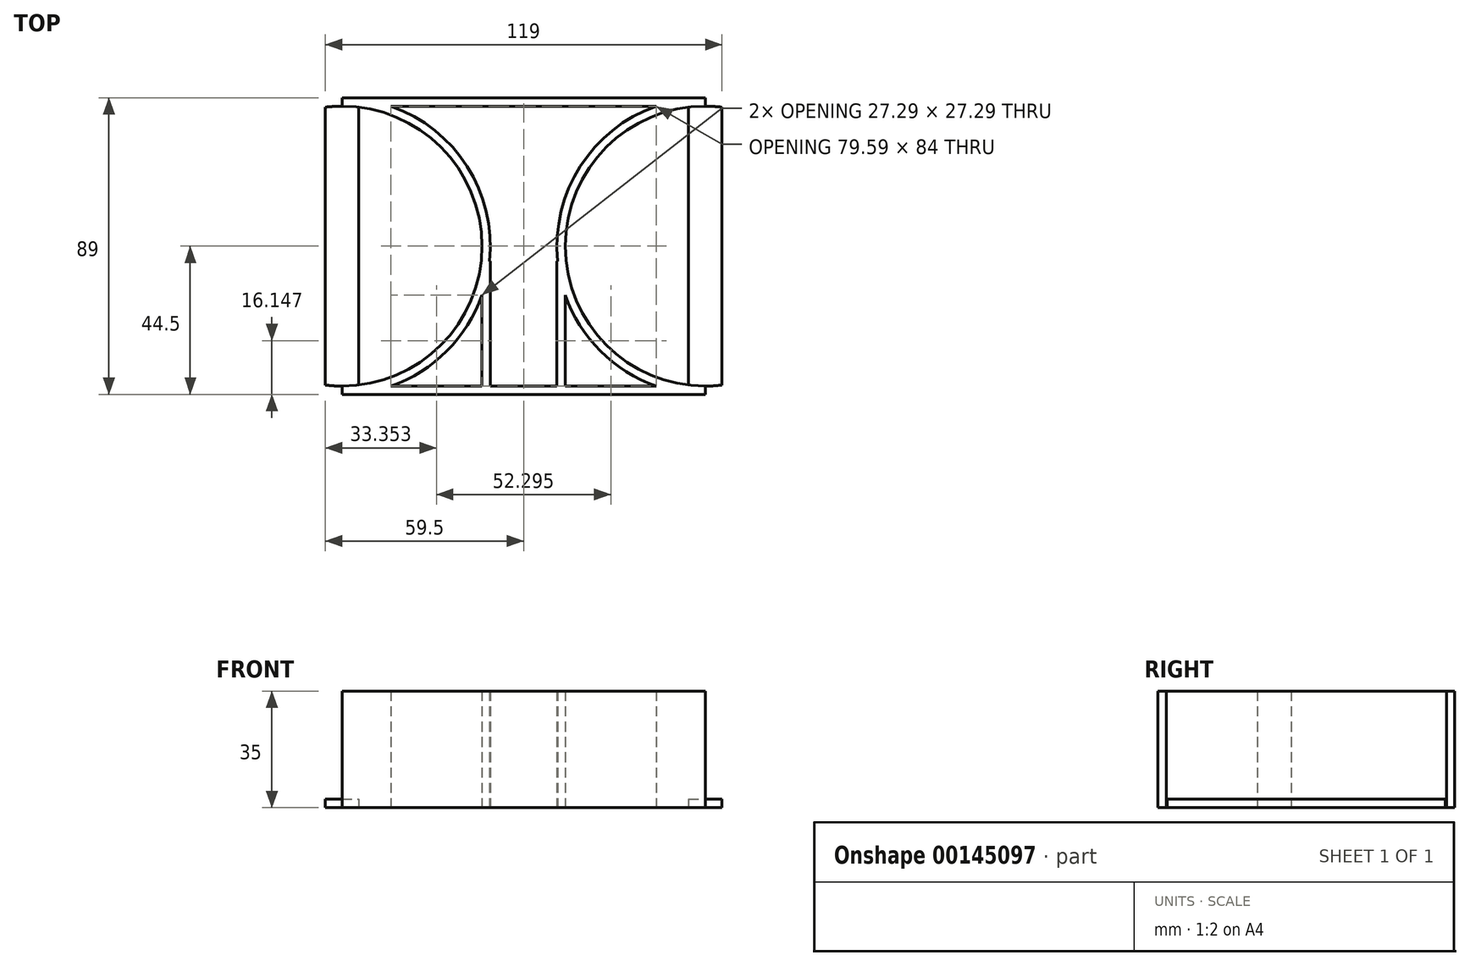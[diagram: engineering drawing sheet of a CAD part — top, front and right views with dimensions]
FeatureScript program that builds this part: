
annotation { "Feature Type Name" : "Feature", "Feature Type Description" : "" }
export const myFeature = defineFeature(function(context is Context, id is Id, definition is map)
    precondition{}
    {
        {
            var Q0;
            Q0=qCreatedBy(makeId("Top.planeOp"),FACE);
            var sketch = newSketch(context, id + "F0", { "sketchPlane" : qUnion([Q0])});
            skLineSegment(sketch, "E0", {"start": v(0, 0) * mm, "end": v(54.5, 0) * mm});
            skLineSegment(sketch, "E1", {"start": v(54.5, 0) * mm, "end": v(54.5, 44.5) * mm});
            skCircle(sketch, "E2", {"center": v(54.5, 44.5) * mm, "radius": 44.5 * mm});
            skCircle(sketch, "E3", {"center": v(54.5, 44.5) * mm, "radius": 42 * mm});
            skLineSegment(sketch, "E4", {"start": v(0, 0) * mm, "end": v(0, 2.5) * mm});
            skLineSegment(sketch, "E5", {"start": v(0, 2.5) * mm, "end": v(54.5, 2.5) * mm});
            skLineSegment(sketch, "E6", {"start": v(0, 0) * mm, "end": v(5, 0) * mm});
            skLineSegment(sketch, "E7", {"start": v(5, 0) * mm, "end": v(10, 0) * mm});
            skLineSegment(sketch, "E8", {"start": v(10, 0) * mm, "end": v(10, 40) * mm});
            skLineSegment(sketch, "E9", {"start": v(10, 0) * mm, "end": v(12.5, 0) * mm});
            skLineSegment(sketch, "E10", {"start": v(12.5, 0) * mm, "end": v(12.5, 40) * mm});
            skLineSegment(sketch, "E11", {"start": v(10, 40) * mm, "end": v(12.5, 40) * mm});
            skLineSegment(sketch, "E12", {"start": v(54.5, 0) * mm, "end": v(54.5, 89) * mm});
            skLineSegment(sketch, "E13", {"start": v(54.5, 89) * mm, "end": v(0, 89) * mm});
            skLineSegment(sketch, "E14", {"start": v(54.5, 86.5) * mm, "end": v(0, 86.5) * mm});
            skLineSegment(sketch, "E15", {"start": v(0, 86.5) * mm, "end": v(0, 89) * mm});
            skLineSegment(sketch, "E16", {"start": v(5, 0) * mm, "end": v(5, 2.5) * mm});
            skLineSegment(sketch, "E17", {"start": v(54.5, 44.5) * mm, "end": v(49.5, 44.5) * mm});
            skLineSegment(sketch, "E18", {"start": v(49.5, 44.5) * mm, "end": v(49.5, 86.2) * mm});
            skLineSegment(sketch, "E19", {"start": v(49.5, 44.5) * mm, "end": v(49.5, 2.8) * mm});
            skLineSegment(sketch, "E20", {"start": v(54.5, 44.5) * mm, "end": v(59.5, 44.5) * mm});
            skLineSegment(sketch, "E21", {"start": v(59.5, 44.5) * mm, "end": v(59.5, 86.2) * mm});
            skLineSegment(sketch, "E22", {"start": v(59.5, 86.2) * mm, "end": v(59.5, 2.8) * mm});
            skSolve(sketch);
        }
        {
            var Q0;
            {var subQ4=sQuery(id+"F0.wireOp",EDGE,"E7");Q0=makeQuery(id+"F0.imprint","IMPRINT",FACE,{"disambiguationData":[TD([[makeQuery(id+"F0.imprint","IMPRINT",EDGE,{"derivedFrom":subQ4}),1.0]])]});}
            var Q1;
            {var subQ5=sQuery(id+"F0.wireOp",EDGE,"E9");Q1=makeQuery(id+"F0.imprint","IMPRINT",FACE,{"disambiguationData":[TD([[makeQuery(id+"F0.imprint","IMPRINT",EDGE,{"derivedFrom":subQ5}),1.0]])]});}
            var Q2;
            {var subQ1=sQuery(id+"F0.wireOp",EDGE,"E2");var subQ7=sQuery(id+"F0.wireOp",EDGE,"E11");var subQ9=makeQuery(id+"F0.imprint","INTERSECT",VERTEX,{"derivedFrom":[subQ1,subQ7]});Q2=makeQuery(id+"F0.imprint","IMPRINT",FACE,{"disambiguationData":[TD([[makeQuery(id+"F0.imprint","IMPRINT",EDGE,{"disambiguationData":[TD([[subQ9,-1.0]])],"derivedFrom":subQ1}),-1.0]])]});}
            var Q3;
            {var subQ0=sQuery(id+"F0.wireOp",EDGE,"E0");Q3=makeQuery(id+"F0.imprint","IMPRINT",FACE,{"disambiguationData":[TD([[makeQuery(id+"F0.imprint","IMPRINT",EDGE,{"derivedFrom":subQ0}),1.0]])]});}
            var Q4;
            {var subQ4=sQuery(id+"F0.wireOp",EDGE,"E2");var subQ6=sQuery(id+"F0.wireOp",EDGE,"E14");var subQ10=makeQuery(id+"F0.imprint","INTERSECT",VERTEX,{"derivedFrom":[subQ4,subQ6]});Q4=makeQuery(id+"F0.imprint","IMPRINT",FACE,{"disambiguationData":[TD([[makeQuery(id+"F0.imprint","IMPRINT",EDGE,{"disambiguationData":[TD([[subQ10,-1.0]])],"derivedFrom":subQ4}),1.0]])]});}
            var Q5;
            {var subQ0=sQuery(id+"F0.wireOp",EDGE,"E11");var subQ1=sQuery(id+"F0.wireOp",EDGE,"E2");var subQ2=makeQuery(id+"F0.imprint","INTERSECT",VERTEX,{"derivedFrom":[subQ1,subQ0]});Q5=makeQuery(id+"F0.imprint","IMPRINT",FACE,{"disambiguationData":[TD([[makeQuery(id+"F0.imprint","IMPRINT",EDGE,{"disambiguationData":[TD([[subQ2,-1.0]])],"derivedFrom":subQ1}),1.0]])]});}
            var Q6;
            {var subQ1=sQuery(id+"F0.wireOp",EDGE,"E2");var subQ3=sQuery(id+"F0.wireOp",EDGE,"E5");var subQ4=makeQuery(id+"F0.imprint","INTERSECT",VERTEX,{"derivedFrom":[subQ1,subQ3]});Q6=makeQuery(id+"F0.imprint","IMPRINT",FACE,{"disambiguationData":[TD([[makeQuery(id+"F0.imprint","IMPRINT",EDGE,{"disambiguationData":[TD([[subQ4,-1.0]])],"derivedFrom":subQ1}),1.0]])]});}
            var Q7;
            {var subQ0=sQuery(id+"F0.wireOp",EDGE,"E12");var subQ1=sQuery(id+"F0.wireOp",EDGE,"E2");var subQ2=makeQuery(id+"F0.imprint","INTERSECT",VERTEX,{"derivedFrom":[sQuery(id+"F0.wireOp",EDGE,"E0"),subQ1,subQ0]});Q7=makeQuery(id+"F0.imprint","IMPRINT",FACE,{"disambiguationData":[TD([[makeQuery(id+"F0.imprint","IMPRINT",EDGE,{"disambiguationData":[TD([[subQ2,-1.0]])],"derivedFrom":subQ1}),1.0]])]});}
            var Q8;
            {var subQ1=sQuery(id+"F0.wireOp",EDGE,"E2");var subQ3=sQuery(id+"F0.wireOp",EDGE,"E14");var subQ4=makeQuery(id+"F0.imprint","INTERSECT",VERTEX,{"derivedFrom":[subQ1,subQ3]});Q8=makeQuery(id+"F0.imprint","IMPRINT",FACE,{"disambiguationData":[TD([[makeQuery(id+"F0.imprint","IMPRINT",EDGE,{"disambiguationData":[TD([[subQ4,1.0]])],"derivedFrom":subQ1}),1.0]])]});}
            var Q9;
            {var subQ0=sQuery(id+"F0.wireOp",EDGE,"E13");Q9=makeQuery(id+"F0.imprint","IMPRINT",FACE,{"disambiguationData":[TD([[makeQuery(id+"F0.imprint","IMPRINT",EDGE,{"derivedFrom":subQ0}),1.0]])]});}
            extrude(context, id + "F1", {"entities" : qUnion([Q0, Q1, Q2, Q3, Q4, Q5, Q6, Q7, Q8, Q9]), "depth" : 35 * mm});
        }
        {
            var Q0;
            {var subQ5=sQuery(id+"F0.wireOp",EDGE,"E20");Q0=makeQuery(id+"F0.imprint","IMPRINT",FACE,{"disambiguationData":[TD([[makeQuery(id+"F0.imprint","IMPRINT",EDGE,{"derivedFrom":subQ5}),1.0]])]});}
            var Q1;
            {var subQ4=sQuery(id+"F0.wireOp",EDGE,"E17");Q1=makeQuery(id+"F0.imprint","IMPRINT",FACE,{"disambiguationData":[TD([[makeQuery(id+"F0.imprint","IMPRINT",EDGE,{"derivedFrom":subQ4}),-1.0]])]});}
            var Q2;
            {var subQ4=sQuery(id+"F0.wireOp",EDGE,"E17");Q2=makeQuery(id+"F0.imprint","IMPRINT",FACE,{"disambiguationData":[TD([[makeQuery(id+"F0.imprint","IMPRINT",EDGE,{"derivedFrom":subQ4}),1.0]])]});}
            var Q3;
            {var subQ5=sQuery(id+"F0.wireOp",EDGE,"E20");Q3=makeQuery(id+"F0.imprint","IMPRINT",FACE,{"disambiguationData":[TD([[makeQuery(id+"F0.imprint","IMPRINT",EDGE,{"derivedFrom":subQ5}),-1.0]])]});}
            extrude(context, id + "F2", {"entities" : qUnion([Q0, Q1, Q2, Q3]), "operationType" : NewBodyOperationType.ADD, "depth" : 2.5 * mm});
        }
        {
            var Q0;
            Q0=makeQuery(id+"F1.opExtrude","SWEPT_BODY",BODY,{"disambiguationData":[OSD([sQuery(id+"F0.wireOp",EDGE,"E0"),sQuery(id+"F0.wireOp",EDGE,"E2"),sQuery(id+"F0.wireOp",EDGE,"E3"),sQuery(id+"F0.wireOp",EDGE,"E5"),sQuery(id+"F0.wireOp",EDGE,"E7"),sQuery(id+"F0.wireOp",EDGE,"E8"),sQuery(id+"F0.wireOp",EDGE,"E9"),sQuery(id+"F0.wireOp",EDGE,"E10"),sQuery(id+"F0.wireOp",EDGE,"E11"),sQuery(id+"F0.wireOp",EDGE,"E13"),sQuery(id+"F0.wireOp",EDGE,"E14"),sQuery(id+"F0.wireOp",EDGE,"E15"),sQuery(id+"F0.wireOp",EDGE,"E16")])]});
            var Q1;
            Q1=qCreatedBy(makeId("Right.planeOp"),FACE);
            mirror(context, id + "F3", {"operationType" : NewBodyOperationType.ADD, "entities" : qUnion([Q0]), "mirrorPlane" : qUnion([Q1])});
        }
    });
